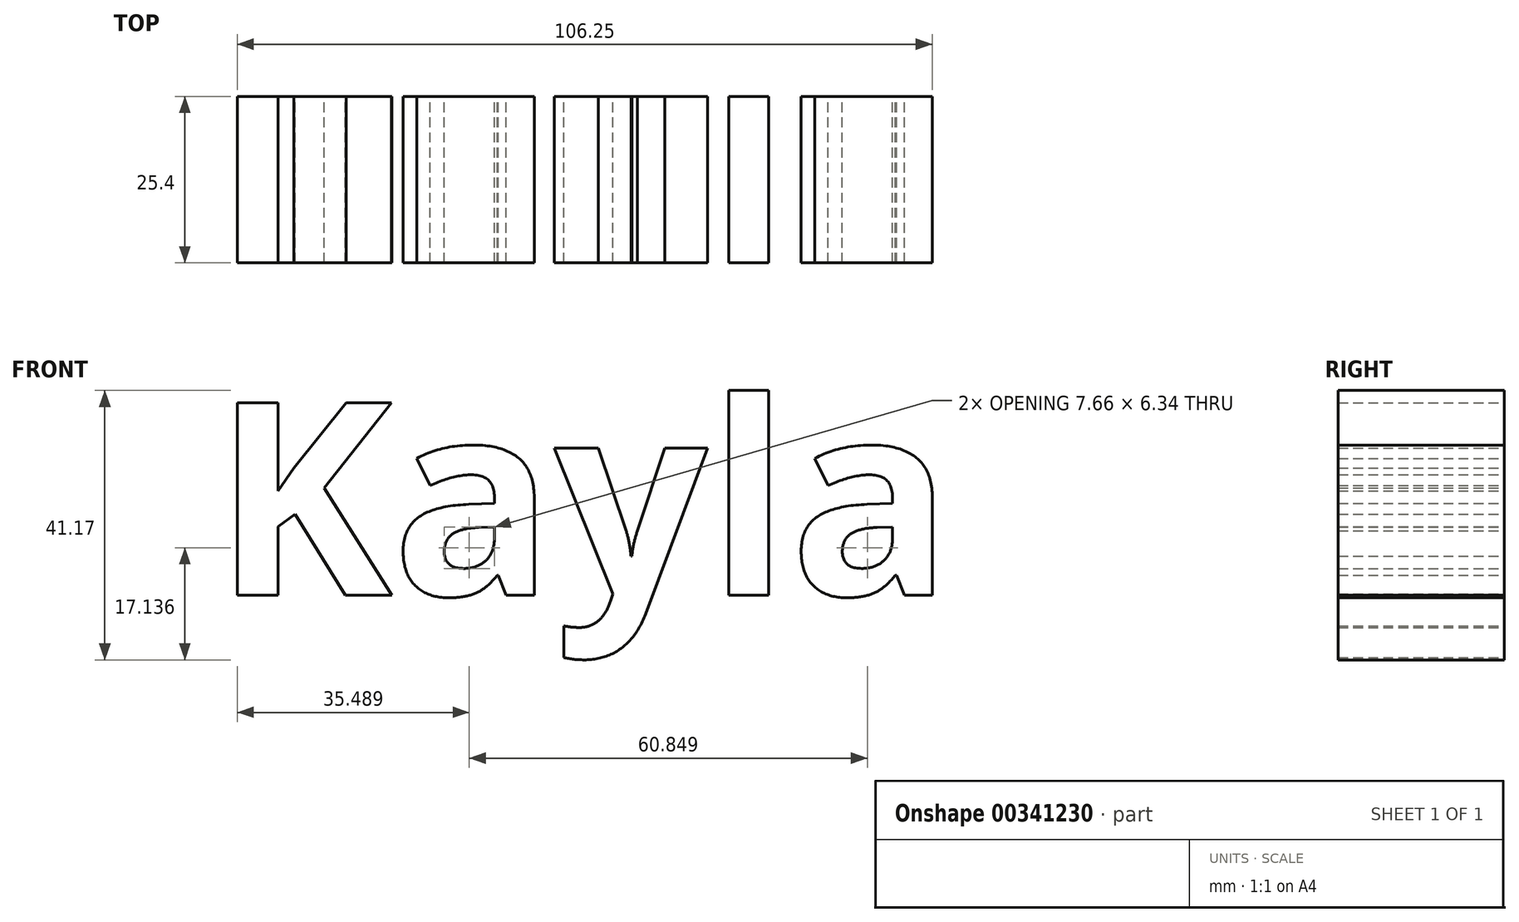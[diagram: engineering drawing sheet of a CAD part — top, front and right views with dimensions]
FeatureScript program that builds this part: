
annotation { "Feature Type Name" : "Feature", "Feature Type Description" : "" }
export const myFeature = defineFeature(function(context is Context, id is Id, definition is map)
    precondition{}
    {
        {
            var Q0;
            Q0=qCreatedBy(makeId("Front.planeOp"),FACE);
            var sketch = newSketch(context, id + "F0", { "sketchPlane" : qUnion([Q0])});
            skText(sketch, "E0", { "text": "Kayla", "fontName": "OpenSans-Bold.ttf"});
            const initialGuessF0  = {"E0": [-0.05727, 0.00835, 1, 0, 0.02964]};
            skSetInitialGuess(sketch, initialGuessF0);
            skSolve(sketch);
        }
        {
            var Q0;
            Q0 = qSketchRegion(id + "F0", true);
            extrude(context, id + "F1", {"entities" : qUnion([Q0]), "depth" : 25.4 * mm});
        }
    });
